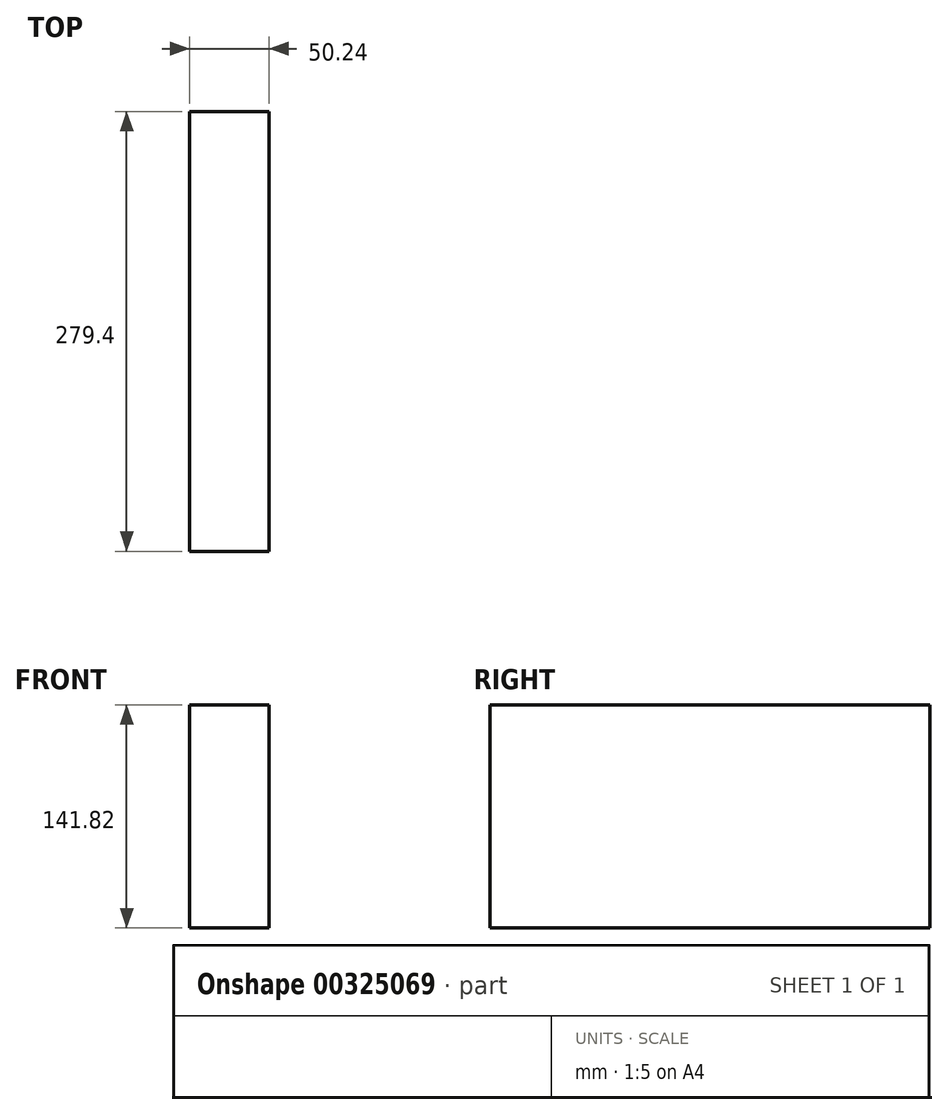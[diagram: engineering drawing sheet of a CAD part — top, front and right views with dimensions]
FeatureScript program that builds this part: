
annotation { "Feature Type Name" : "Feature", "Feature Type Description" : "" }
export const myFeature = defineFeature(function(context is Context, id is Id, definition is map)
    precondition{}
    {
        {
            var Q0;
            Q0=qCreatedBy(makeId("Front.planeOp"),FACE);
            var sketch = newSketch(context, id + "F0", { "sketchPlane" : qUnion([Q0])});
            skLineSegment(sketch, "E0.bottom", {"start": v(25.12, -70.9) * mm, "end": v(-25.12, -70.9) * mm});
            skLineSegment(sketch, "E0.top", {"start": v(25.12, 70.9) * mm, "end": v(-25.12, 70.9) * mm});
            skLineSegment(sketch, "E0.left", {"start": v(25.12, -70.9) * mm, "end": v(25.12, 70.9) * mm});
            skLineSegment(sketch, "E0.right", {"start": v(-25.12, -70.9) * mm, "end": v(-25.12, 70.9) * mm});
            skPoint(sketch, "E0.middle", {"position": v(0, 0) * mm});
            skSolve(sketch);
        }
        {
            var Q0;
            Q0 = qSketchRegion(id + "F0", true);
            extrude(context, id + "F1", {"entities" : qUnion([Q0]), "endBound" : BoundingType.SYMMETRIC, "depth" : 279.4 * mm});
        }
    });
